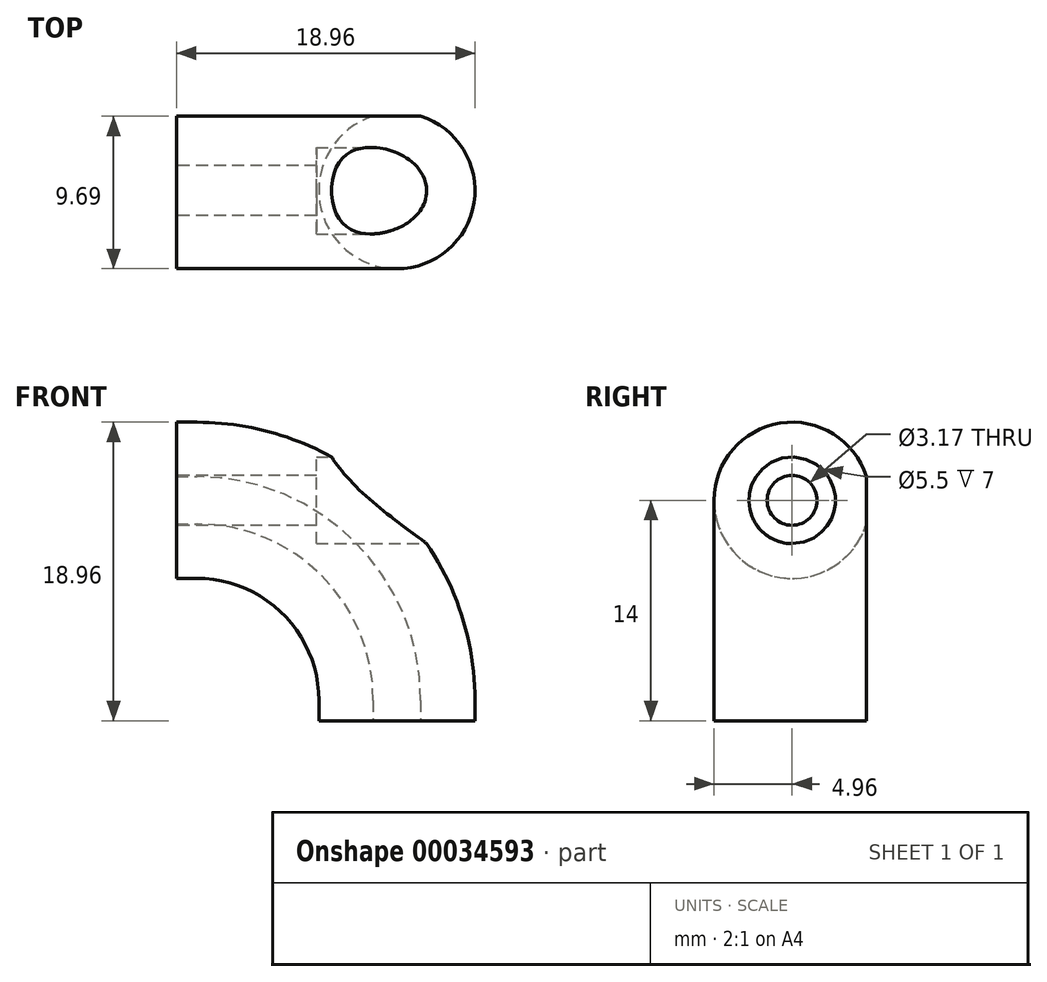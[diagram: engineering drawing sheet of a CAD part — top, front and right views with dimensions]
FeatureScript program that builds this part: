
annotation { "Feature Type Name" : "Feature", "Feature Type Description" : "" }
export const myFeature = defineFeature(function(context is Context, id is Id, definition is map)
    precondition{}
    {
        {
            var Q0;
            Q0=qCreatedBy(makeId("Front.planeOp"),FACE);
            var sketch = newSketch(context, id + "F0", { "sketchPlane" : qUnion([Q0])});
            skLineSegment(sketch, "E0", {"start": v(0, 0) * mm, "end": v(1.3, 0) * mm});
            skLineSegment(sketch, "E1", {"start": v(14, -12.7) * mm, "end": v(14, -14) * mm});
            skPoint(sketch, "E2.visualSharp", {"position": v(14, 0) * mm});
            skArc(sketch, "E2.filletArc", {"start": v(14, -12.7) * mm, "mid": v(10.28, -3.72) * mm, "end": v(1.3, 0) * mm});
            skSolve(sketch);
        }
        {
            var Q0;
            Q0=qCreatedBy(makeId("Right.planeOp"),FACE);
            var sketch = newSketch(context, id + "F1", { "sketchPlane" : qUnion([Q0])});
            skCircle(sketch, "E3", {"center": v(0, 0) * mm, "radius": 4.96 * mm});
            skSolve(sketch);
        }
        {
            var Q0;
            Q0=makeQuery(id+"F1.imprint","IMPRINT",FACE,{"disambiguationData":[TD([[makeQuery(id+"F1.imprint","IMPRINT",EDGE,{"derivedFrom":sQuery(id+"F1.wireOp",EDGE,"E3")}),1.0]])]});
            var Q1;
            Q1=sQuery(id+"F0.wireOp",EDGE,"E0");
            var Q2;
            Q2=sQuery(id+"F0.wireOp",EDGE,"E2.filletArc");
            var Q3;
            Q3=sQuery(id+"F0.wireOp",EDGE,"E1");
            sweep(context, id + "F2", {"profiles" : qUnion([Q0]), "path" : qUnion([Q1, Q2, Q3])});
        }
        {
            var Q0;
            Q0=makeQuery(id+"F2.opSweep","CAP_FACE",FACE,{"disambiguationData":[OSD([sQuery(id+"F0.wireOp",VERTEX,"E0.start"),sQuery(id+"F1.wireOp",EDGE,"E3")])],"isStart":true});
            var sketch = newSketch(context, id + "F3", { "sketchPlane" : qUnion([Q0])});
            skCircle(sketch, "E4", {"center": v(0, 0) * mm, "radius": 1.59 * mm});
            skSolve(sketch);
        }
        {
            var Q0;
            Q0 = qSketchRegion(id + "F3", true);
            extrude(context, id + "F4", {"entities" : qUnion([Q0]), "operationType" : NewBodyOperationType.REMOVE, "endBound" : BoundingType.THROUGH_ALL, "oppositeDirection" : true, "depth" : 25.4 * mm});
        }
        {
            var Q0;
            Q0=qCreatedBy(makeId("Right.planeOp"),FACE);
            cPlane(context, id + "F5", {"entities" : qUnion([Q0]), "cplaneType" : CPlaneType.OFFSET, "offset" : 19.05 * mm, "width" : 152.4 * mm, "height" : 152.4 * mm});
        }
        {
            var Q0;
            Q0=qCreatedBy(id+"F5.planeOp",FACE);
            var sketch = newSketch(context, id + "F6", { "sketchPlane" : qUnion([Q0])});
            skCircle(sketch, "E5", {"center": v(0, 0) * mm, "radius": 2.75 * mm});
            skSolve(sketch);
        }
        {
            var Q0;
            Q0 = qSketchRegion(id + "F6", true);
            extrude(context, id + "F7", {"entities" : qUnion([Q0]), "operationType" : NewBodyOperationType.REMOVE, "oppositeDirection" : true, "depth" : 10.16 * mm});
        }
        {
            var Q0;
            Q0=qCreatedBy(makeId("Front.planeOp"),FACE);
            var sketch = newSketch(context, id + "F8", { "sketchPlane" : qUnion([Q0])});
            skLineSegment(sketch, "E6", {"start": v(14, -14) * mm, "end": v(14, -19.15) * mm, "construction": true});
            skLineSegment(sketch, "E7", {"start": v(14, -14) * mm, "end": v(10.19, -14) * mm});
            skArc(sketch, "E8", {"start": v(10.2, -14) * mm, "mid": v(7.6, -18.84) * mm, "end": v(9.71, -23.9) * mm});
            skArc(sketch, "E9.0", {"start": v(13.7, -15.3) * mm, "mid": v(10.34, -17.9) * mm, "end": v(11.42, -22.03) * mm});
            skLineSegment(sketch, "E10", {"start": v(13.7, -15.3) * mm, "end": v(14, -15.3) * mm});
            skLineSegment(sketch, "E11", {"start": v(11.42, -22.03) * mm, "end": v(9.71, -23.9) * mm});
            skLineSegment(sketch, "E12.MirrorCS", {"start": v(14.3, -15.3) * mm, "end": v(14, -15.3) * mm});
            skLineSegment(sketch, "E13.MirrorCS", {"start": v(14, -14) * mm, "end": v(17.8, -14) * mm});
            skArc(sketch, "E14.MirrorCS", {"start": v(17.8, -14) * mm, "mid": v(20.4, -18.84) * mm, "end": v(18.29, -23.9) * mm});
            skArc(sketch, "E15.MirrorCS", {"start": v(14.3, -15.3) * mm, "mid": v(17.66, -17.9) * mm, "end": v(16.58, -22.03) * mm});
            skLineSegment(sketch, "E16.MirrorCS", {"start": v(16.58, -22.03) * mm, "end": v(18.29, -23.9) * mm});
            skSolve(sketch);
        }
        {
            var Q0;
            Q0=qCreatedBy(makeId("Right.planeOp"),FACE);
            var sketch = newSketch(context, id + "F9", { "sketchPlane" : qUnion([Q0])});
            skLineSegment(sketch, "E17.bottom", {"start": v(4.98, -14) * mm, "end": v(4.73, -14) * mm});
            skLineSegment(sketch, "E17.top", {"start": v(4.98, 5.05) * mm, "end": v(4.73, 5.05) * mm});
            skLineSegment(sketch, "E17.left", {"start": v(4.98, -14) * mm, "end": v(4.98, 5.05) * mm});
            skLineSegment(sketch, "E17.right", {"start": v(4.73, -14) * mm, "end": v(4.73, 5.05) * mm});
            skSolve(sketch);
        }
        {
            var Q0;
            Q0 = qSketchRegion(id + "F9", true);
            extrude(context, id + "F10", {"entities" : qUnion([Q0]), "operationType" : NewBodyOperationType.REMOVE, "endBound" : BoundingType.THROUGH_ALL, "depth" : 25.4 * mm});
        }
    });
